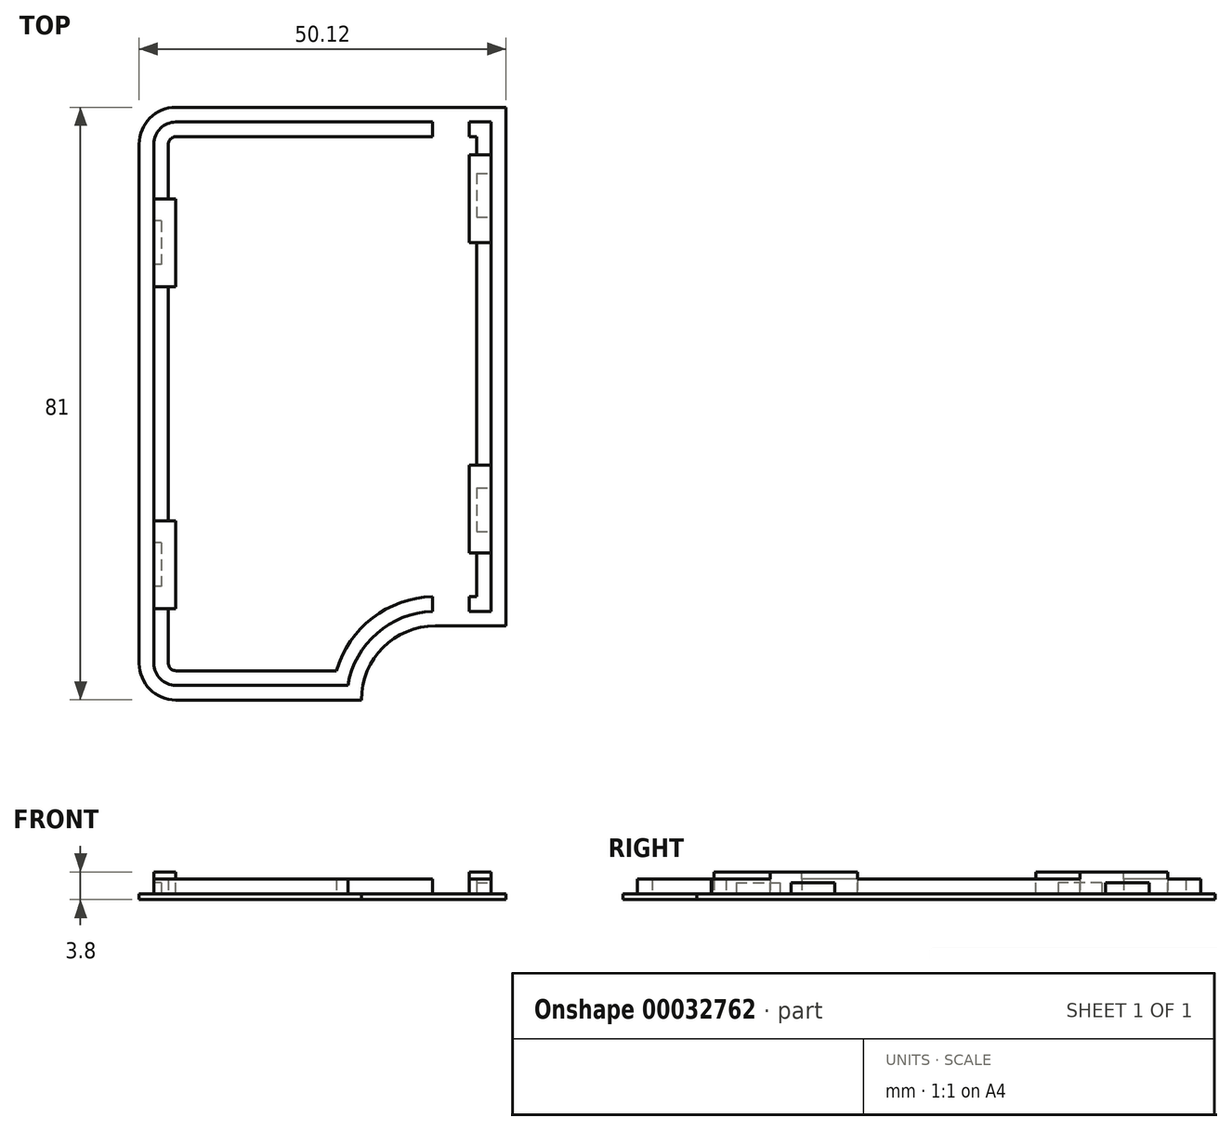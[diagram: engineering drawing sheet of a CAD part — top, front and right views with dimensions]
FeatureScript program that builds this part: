
annotation { "Feature Type Name" : "Feature", "Feature Type Description" : "" }
export const myFeature = defineFeature(function(context is Context, id is Id, definition is map)
    precondition{}
    {
        {
            var Q0;
            Q0=qCreatedBy(makeId("Top.planeOp"),FACE);
            var sketch = newSketch(context, id + "F0", { "sketchPlane" : qUnion([Q0])});
            skLineSegment(sketch, "E0.right", {"start": v(-29.22, 49.84) * mm, "end": v(-29.22, -31.16) * mm});
            skLineSegment(sketch, "E1.MirrorCS", {"start": v(11.28, -21.04) * mm, "end": v(20.9, -21.04) * mm});
            skLineSegment(sketch, "E2.MirrorCS", {"start": v(20.9, 49.84) * mm, "end": v(20.9, -21.04) * mm});
            skArc(sketch, "E3.MirrorCS", {"start": v(1.16, -31.16) * mm, "mid": v(4.12, -24) * mm, "end": v(11.28, -21.04) * mm});
            skLineSegment(sketch, "E4.MirrorCS", {"start": v(-29.22, 49.84) * mm, "end": v(20.9, 49.84) * mm});
            skLineSegment(sketch, "E5.MirrorCS", {"start": v(1.16, -31.16) * mm, "end": v(-29.22, -31.16) * mm});
            skSolve(sketch);
        }
        {
            var Q0;
            Q0=makeQuery(id+"F0.imprint","IMPRINT",FACE,{"disambiguationData":[TD([[makeQuery(id+"F0.imprint","IMPRINT",EDGE,{"derivedFrom":sQuery(id+"F0.wireOp",EDGE,"E0.right")}),1.0]])]});
            extrude(context, id + "F1", {"entities" : qUnion([Q0]), "depth" : .8 * mm});
        }
        {
            var Q0;
            Q0=makeQuery(id+"F1.opExtrude","SWEPT_EDGE",EDGE,{"disambiguationData":[OSD([sQuery(id+"F0.wireOp",EDGE,"E0.right"),sQuery(id+"F0.wireOp",EDGE,"E4.MirrorCS")])]});
            fillet(context, id + "F2", {"entities" : qUnion([Q0]), "radius" : 5 * mm, "tangentPropagation" : true, "allowEdgeOverflow" : false});
        }
        {
            var Q0;
            Q0=makeQuery(id+"F1.opExtrude","SWEPT_EDGE",EDGE,{"disambiguationData":[OSD([sQuery(id+"F0.wireOp",EDGE,"E0.right"),sQuery(id+"F0.wireOp",EDGE,"E5.MirrorCS")])]});
            fillet(context, id + "F3", {"entities" : qUnion([Q0]), "radius" : 5 * mm, "tangentPropagation" : true, "allowEdgeOverflow" : false});
        }
        {
            var Q0;
            Q0=makeQuery(id+"F1.opExtrude","CAP_FACE",FACE,{"disambiguationData":[OSD([sQuery(id+"F0.wireOp",EDGE,"E0.right"),sQuery(id+"F0.wireOp",EDGE,"E1.MirrorCS"),sQuery(id+"F0.wireOp",EDGE,"E2.MirrorCS"),sQuery(id+"F0.wireOp",EDGE,"E3.MirrorCS"),sQuery(id+"F0.wireOp",EDGE,"E4.MirrorCS"),sQuery(id+"F0.wireOp",EDGE,"E5.MirrorCS")])],"isStart":false});
            var sketch = newSketch(context, id + "F4", { "sketchPlane" : qUnion([Q0])});
            skLineSegment(sketch, "E6.0", {"start": v(-27.22, 44.84) * mm, "end": v(-27.22, -26.16) * mm});
            skArc(sketch, "E6.1", {"start": v(-24.22, 47.84) * mm, "mid": v(-26.34, 46.96) * mm, "end": v(-27.22, 44.84) * mm});
            skLineSegment(sketch, "E6.2", {"start": v(-24.22, 47.84) * mm, "end": v(18.9, 47.84) * mm});
            skLineSegment(sketch, "E6.3", {"start": v(18.9, 47.84) * mm, "end": v(18.9, -19.04) * mm});
            skLineSegment(sketch, "E6.4", {"start": v(11.28, -19.04) * mm, "end": v(18.9, -19.04) * mm});
            skArc(sketch, "E6.5", {"start": v(-27.22, -26.16) * mm, "mid": v(-26.34, -28.28) * mm, "end": v(-24.22, -29.16) * mm});
            skArc(sketch, "E6.6", {"start": v(-0.68, -29.16) * mm, "mid": v(3.45, -21.9) * mm, "end": v(11.28, -19.04) * mm});
            skLineSegment(sketch, "E6.7", {"start": v(-0.68, -29.16) * mm, "end": v(-24.22, -29.16) * mm});
            skSolve(sketch);
        }
        {
            var Q0;
            Q0=makeQuery(id+"F4.imprint","IMPRINT",FACE,{"disambiguationData":[TD([[makeQuery(id+"F4.imprint","IMPRINT",EDGE,{"derivedFrom":sQuery(id+"F4.wireOp",EDGE,"E6.0")}),1.0]])]});
            extrude(context, id + "F5", {"entities" : qUnion([Q0]), "operationType" : NewBodyOperationType.ADD, "depth" : 3 * mm});
        }
        {
            var Q0;
            Q0=makeQuery(id+"F5.opExtrude","SWEPT_FACE",FACE,{"disambiguationData":[OSD([sQuery(id+"F4.wireOp",EDGE,"E6.0")])]});
            var sketch = newSketch(context, id + "F6", { "sketchPlane" : qUnion([Q0])});
            skLineSegment(sketch, "E7", {"start": v(-9.34, 0.8) * mm, "end": v(-9.34, 3.8) * mm, "construction": true});
            skLineSegment(sketch, "E8", {"start": v(-9.34, 2.3) * mm, "end": v(-28.34, 2.3) * mm, "construction": true});
            skLineSegment(sketch, "E9", {"start": v(-9.34, 2.3) * mm, "end": v(9.66, 2.3) * mm, "construction": true});
            skLineSegment(sketch, "E10.bottom", {"start": v(-34.34, 2.3) * mm, "end": v(-28.34, 2.3) * mm});
            skLineSegment(sketch, "E10.top", {"start": v(-34.34, 0.8) * mm, "end": v(-28.34, 0.8) * mm});
            skLineSegment(sketch, "E10.left", {"start": v(-34.34, 2.3) * mm, "end": v(-34.34, 0.8) * mm});
            skLineSegment(sketch, "E10.right", {"start": v(-28.34, 2.3) * mm, "end": v(-28.34, 0.8) * mm});
            skLineSegment(sketch, "E11.bottom", {"start": v(15.66, 2.3) * mm, "end": v(9.66, 2.3) * mm});
            skLineSegment(sketch, "E11.top", {"start": v(15.66, 0.8) * mm, "end": v(9.66, 0.8) * mm});
            skLineSegment(sketch, "E11.left", {"start": v(15.66, 2.3) * mm, "end": v(15.66, 0.8) * mm});
            skLineSegment(sketch, "E11.right", {"start": v(9.66, 2.3) * mm, "end": v(9.66, 0.8) * mm});
            skSolve(sketch);
        }
        {
            var Q0;
            Q0=makeQuery(id+"F5.opExtrude","SWEPT_FACE",FACE,{"disambiguationData":[OSD([sQuery(id+"F4.wireOp",EDGE,"E6.3")])]});
            var sketch = newSketch(context, id + "F7", { "sketchPlane" : qUnion([Q0])});
            skSolve(sketch);
        }
        {
            var Q0;
            {var subQ0=sQuery(id+"F4.wireOp",EDGE,"E6.3");Q0=makeQuery(id+"F7.imprint","IMPRINT",FACE,{"disambiguationData":[TD([[makeQuery(id+"F7.imprint","IMPRINT",EDGE,{"derivedFrom":makeQuery(id+"F5.opExtrude","CAP_EDGE",EDGE,{"disambiguationData":[OSD([subQ0])],"isStart":false})}),1.0]])]});}
            var sketch = newSketch(context, id + "F8", { "sketchPlane" : qUnion([Q0])});
            skLineSegment(sketch, "E12.bottom", {"start": v(-8.16, 2.3) * mm, "end": v(-2.16, 2.3) * mm});
            skLineSegment(sketch, "E12.top", {"start": v(-8.16, 0.8) * mm, "end": v(-2.16, 0.8) * mm});
            skLineSegment(sketch, "E12.left", {"start": v(-8.16, 2.3) * mm, "end": v(-8.16, 0.8) * mm});
            skLineSegment(sketch, "E12.right", {"start": v(-2.16, 2.3) * mm, "end": v(-2.16, 0.8) * mm});
            skLineSegment(sketch, "E13.bottom", {"start": v(34.84, 2.3) * mm, "end": v(40.84, 2.3) * mm});
            skLineSegment(sketch, "E13.top", {"start": v(34.84, 0.8) * mm, "end": v(40.84, 0.8) * mm});
            skLineSegment(sketch, "E13.left", {"start": v(34.84, 2.3) * mm, "end": v(34.84, 0.8) * mm});
            skLineSegment(sketch, "E13.right", {"start": v(40.84, 2.3) * mm, "end": v(40.84, 0.8) * mm});
            skSolve(sketch);
        }
        {
            var Q0;
            Q0 = qSketchRegion(id + "F8", true);
            extrude(context, id + "F9", {"entities" : qUnion([Q0]), "operationType" : NewBodyOperationType.REMOVE, "oppositeDirection" : true, "depth" : 2 * mm});
        }
        {
            var Q0;
            Q0=makeQuery(id+"F5.opExtrude","CAP_FACE",FACE,{"disambiguationData":[OSD([sQuery(id+"F4.wireOp",EDGE,"E6.0"),sQuery(id+"F4.wireOp",EDGE,"E6.1"),sQuery(id+"F4.wireOp",EDGE,"E6.2"),sQuery(id+"F4.wireOp",EDGE,"E6.3"),sQuery(id+"F4.wireOp",EDGE,"E6.4"),sQuery(id+"F4.wireOp",EDGE,"E6.5"),sQuery(id+"F4.wireOp",EDGE,"E6.6"),sQuery(id+"F4.wireOp",EDGE,"E6.7")])],"isStart":false});
            var sketch = newSketch(context, id + "F10", { "sketchPlane" : qUnion([Q0])});
            skLineSegment(sketch, "E14.bottom", {"start": v(-27.22, -18.66) * mm, "end": v(-24.22, -18.66) * mm});
            skLineSegment(sketch, "E14.top", {"start": v(-27.22, -6.66) * mm, "end": v(-24.22, -6.66) * mm});
            skLineSegment(sketch, "E14.right", {"start": v(-24.22, -18.66) * mm, "end": v(-24.22, -6.66) * mm});
            skLineSegment(sketch, "E15.bottom", {"start": v(-27.22, 25.34) * mm, "end": v(-24.22, 25.34) * mm});
            skLineSegment(sketch, "E15.top", {"start": v(-27.22, 37.34) * mm, "end": v(-24.22, 37.34) * mm});
            skLineSegment(sketch, "E15.right", {"start": v(-24.22, 25.34) * mm, "end": v(-24.22, 37.34) * mm});
            skLineSegment(sketch, "E16.bottom", {"start": v(15.9, -11.04) * mm, "end": v(18.9, -11.04) * mm});
            skLineSegment(sketch, "E16.top", {"start": v(15.9, 0.96) * mm, "end": v(18.9, 0.96) * mm});
            skLineSegment(sketch, "E16.left", {"start": v(15.9, -11.04) * mm, "end": v(15.9, 0.96) * mm});
            skLineSegment(sketch, "E17.bottom", {"start": v(15.9, 31.34) * mm, "end": v(18.9, 31.34) * mm});
            skLineSegment(sketch, "E17.top", {"start": v(15.9, 43.34) * mm, "end": v(18.9, 43.34) * mm});
            skLineSegment(sketch, "E17.left", {"start": v(15.9, 31.34) * mm, "end": v(15.9, 43.34) * mm});
            skSolve(sketch);
        }
        {
            var Q0;
            {var subQ6=sQuery(id+"F10.wireOp",EDGE,"E14.bottom");Q0=makeQuery(id+"F10.imprint","IMPRINT",FACE,{"disambiguationData":[TD([[makeQuery(id+"F10.imprint","IMPRINT",EDGE,{"derivedFrom":subQ6}),-1.0]])]});}
            extrude(context, id + "F11", {"entities" : qUnion([Q0]), "operationType" : NewBodyOperationType.REMOVE, "oppositeDirection" : true, "depth" : 1.5 * mm});
        }
        {
            var Q0;
            {var subQ0=sQuery(id+"F4.wireOp",EDGE,"E6.2");var subQ1=sQuery(id+"F4.wireOp",EDGE,"E6.4");var subQ2=sQuery(id+"F10.wireOp",EDGE,"E17.top");var subQ3=sQuery(id+"F10.wireOp",EDGE,"E17.left");var subQ4=sQuery(id+"F4.wireOp",EDGE,"E6.3");var subQ5=sQuery(id+"F10.wireOp",EDGE,"E16.left");var subQ6=sQuery(id+"F10.wireOp",EDGE,"E16.top");var subQ7=sQuery(id+"F10.wireOp",EDGE,"E17.bottom");var subQ8=sQuery(id+"F10.wireOp",EDGE,"E16.bottom");Q0=makeQuery(id+"FbkqSHNZKuOhvot_1.boolean.opBoolean","SPLIT",FACE,{"disambiguationData":[TD([makeQuery(id+"F5.opExtrude","SWEPT_FACE",FACE,{"disambiguationData":[OSD([subQ4])]})])],"derivedFrom":makeQuery(id+"F11.boolean.opBoolean","COPY",FACE,{"derivedFrom":makeQuery(id+"F11.opExtrude","CAP_FACE",FACE,{"disambiguationData":[OSD([sQuery(id+"F4.wireOp",EDGE,"E6.0"),sQuery(id+"F4.wireOp",EDGE,"E6.1"),subQ0,subQ4,subQ1,sQuery(id+"F4.wireOp",EDGE,"E6.5"),sQuery(id+"F4.wireOp",EDGE,"E6.6"),sQuery(id+"F4.wireOp",EDGE,"E6.7"),sQuery(id+"F10.wireOp",EDGE,"E14.bottom"),sQuery(id+"F10.wireOp",EDGE,"E14.top"),sQuery(id+"F10.wireOp",EDGE,"E14.right"),sQuery(id+"F10.wireOp",EDGE,"E15.bottom"),sQuery(id+"F10.wireOp",EDGE,"E15.top"),sQuery(id+"F10.wireOp",EDGE,"E15.right"),subQ8,subQ6,subQ5,subQ7,subQ2,subQ3])],"isStart":false})})});}
            var Q1;
            {var subQ2=sQuery(id+"F8.wireOp",EDGE,"E13.top");var subQ3=sQuery(id+"F0.wireOp",EDGE,"E3.MirrorCS");var subQ4=sQuery(id+"F0.wireOp",EDGE,"E2.MirrorCS");var subQ5=sQuery(id+"F0.wireOp",EDGE,"E1.MirrorCS");var subQ6=sQuery(id+"F0.wireOp",EDGE,"E0.right");var subQ7=sQuery(id+"F0.wireOp",EDGE,"E4.MirrorCS");var subQ8=sQuery(id+"F0.wireOp",EDGE,"E5.MirrorCS");Q1=makeQuery(id+"FbkqSHNZKuOhvot_1.boolean.opBoolean","MERGE",FACE,{"derivedFrom":[makeQuery(id+"F1ftWp3afHHN7Bv_1.boolean.opBoolean","SPLIT",FACE,{"disambiguationData":[TD([makeQuery(id+"F1.opExtrude","SWEPT_FACE",FACE,{"disambiguationData":[OSD([subQ6])]})])],"derivedFrom":makeQuery(id+"F9.boolean.opBoolean","MERGE",FACE,{"derivedFrom":[makeQuery(id+"F1.opExtrude","CAP_FACE",FACE,{"disambiguationData":[OSD([subQ6,subQ5,subQ4,subQ3,subQ7,subQ8])],"isStart":false}),makeQuery(id+"F9.opExtrude","SWEPT_FACE",FACE,{"disambiguationData":[OSD([sQuery(id+"F8.wireOp",EDGE,"E12.top")])]}),makeQuery(id+"F9.opExtrude","SWEPT_FACE",FACE,{"disambiguationData":[OSD([subQ2])]})]})}),makeQuery(id+"FbkqSHNZKuOhvot_1.opExtrude","CAP_FACE",FACE,{"disambiguationData":[OSD([sQuery(id+"FVtTkqiu5xKcEQb_1.wireOp",EDGE,"mb8N7D4M-YfVz-ZY3y-VdnK-RlEoSl1ozBKI.bottom"),sQuery(id+"FVtTkqiu5xKcEQb_1.wireOp",EDGE,"mb8N7D4M-YfVz-ZY3y-VdnK-RlEoSl1ozBKI.top"),sQuery(id+"FVtTkqiu5xKcEQb_1.wireOp",EDGE,"mb8N7D4M-YfVz-ZY3y-VdnK-RlEoSl1ozBKI.left"),sQuery(id+"FVtTkqiu5xKcEQb_1.wireOp",EDGE,"mb8N7D4M-YfVz-ZY3y-VdnK-RlEoSl1ozBKI.right")])],"isStart":false})]});}
            extrude(context, id + "F12", {"entities" : qUnion([Q0]), "operationType" : NewBodyOperationType.REMOVE, "endBound" : BoundingType.UP_TO_SURFACE, "oppositeDirection" : true, "endBoundEntityFace" : qUnion([Q1]), "depth" : 25 * mm});
        }
        {
            var Q0;
            Q0 = qSketchRegion(id + "F6", true);
            extrude(context, id + "F13", {"entities" : qUnion([Q0]), "operationType" : NewBodyOperationType.REMOVE, "oppositeDirection" : true, "depth" : 1 * mm});
        }
        {
            var Q0;
            Q0=makeQuery(id+"F13.boolean.opBoolean","MERGE",FACE,{"derivedFrom":[makeQuery(id+"F12.boolean.opBoolean","MERGE",FACE,{"derivedFrom":[makeQuery(id+"F9.boolean.opBoolean","MERGE",FACE,{"derivedFrom":[makeQuery(id+"F1.opExtrude","CAP_FACE",FACE,{"disambiguationData":[OSD([sQuery(id+"F0.wireOp",EDGE,"E0.right"),sQuery(id+"F0.wireOp",EDGE,"E1.MirrorCS"),sQuery(id+"F0.wireOp",EDGE,"E2.MirrorCS"),sQuery(id+"F0.wireOp",EDGE,"E3.MirrorCS"),sQuery(id+"F0.wireOp",EDGE,"E4.MirrorCS"),sQuery(id+"F0.wireOp",EDGE,"E5.MirrorCS")])],"isStart":false}),makeQuery(id+"F9.opExtrude","SWEPT_FACE",FACE,{"disambiguationData":[OSD([sQuery(id+"F8.wireOp",EDGE,"E12.top")])]}),makeQuery(id+"F9.opExtrude","SWEPT_FACE",FACE,{"disambiguationData":[OSD([sQuery(id+"F8.wireOp",EDGE,"E13.top")])]})]}),makeQuery(id+"F12.opExtrude","CAP_FACE",FACE,{"disambiguationData":[OSD([sQuery(id+"F4.wireOp",EDGE,"E6.0"),sQuery(id+"F4.wireOp",EDGE,"E6.1"),sQuery(id+"F4.wireOp",EDGE,"E6.2"),sQuery(id+"F4.wireOp",EDGE,"E6.3"),sQuery(id+"F4.wireOp",EDGE,"E6.4"),sQuery(id+"F4.wireOp",EDGE,"E6.5"),sQuery(id+"F4.wireOp",EDGE,"E6.6"),sQuery(id+"F4.wireOp",EDGE,"E6.7"),sQuery(id+"F10.wireOp",EDGE,"E14.bottom"),sQuery(id+"F10.wireOp",EDGE,"E14.top"),sQuery(id+"F10.wireOp",EDGE,"E14.right"),sQuery(id+"F10.wireOp",EDGE,"E15.bottom"),sQuery(id+"F10.wireOp",EDGE,"E15.top"),sQuery(id+"F10.wireOp",EDGE,"E15.right"),sQuery(id+"F10.wireOp",EDGE,"E16.bottom"),sQuery(id+"F10.wireOp",EDGE,"E16.top"),sQuery(id+"F10.wireOp",EDGE,"E16.left"),sQuery(id+"F10.wireOp",EDGE,"E17.bottom"),sQuery(id+"F10.wireOp",EDGE,"E17.top"),sQuery(id+"F10.wireOp",EDGE,"E17.left")])],"isStart":false})]}),makeQuery(id+"F13.opExtrude","SWEPT_FACE",FACE,{"disambiguationData":[OSD([sQuery(id+"F6.wireOp",EDGE,"E10.top")])]}),makeQuery(id+"F13.opExtrude","SWEPT_FACE",FACE,{"disambiguationData":[OSD([sQuery(id+"F6.wireOp",EDGE,"E11.top")])]})]});
            var sketch = newSketch(context, id + "F14", { "sketchPlane" : qUnion([Q0])});
            skLineSegment(sketch, "E18.0", {"start": v(-0.68, -29.16) * mm, "end": v(-24.22, -29.16) * mm});
            skLineSegment(sketch, "E19.0", {"start": v(15.9, -19.04) * mm, "end": v(18.9, -19.04) * mm});
            skLineSegment(sketch, "E20.0", {"start": v(18.9, 47.84) * mm, "end": v(18.9, 43.34) * mm});
            skLineSegment(sketch, "E21.0", {"start": v(-24.22, 47.84) * mm, "end": v(10.9, 47.84) * mm});
            skLineSegment(sketch, "E22.0", {"start": v(-27.22, 44.84) * mm, "end": v(-27.22, 37.34) * mm});
            skArc(sketch, "E23.0", {"start": v(-27.22, -26.16) * mm, "mid": v(-26.34, -28.28) * mm, "end": v(-24.22, -29.16) * mm});
            skArc(sketch, "E24.0", {"start": v(-24.22, 47.84) * mm, "mid": v(-26.34, 46.96) * mm, "end": v(-27.22, 44.84) * mm});
            skLineSegment(sketch, "E25.trimOffspring", {"start": v(-27.22, -18.66) * mm, "end": v(-27.22, -26.16) * mm});
            skLineSegment(sketch, "E26.0", {"start": v(-2.26, -27.16) * mm, "end": v(-24.22, -27.16) * mm});
            skLineSegment(sketch, "E27.0", {"start": v(15.9, -17.04) * mm, "end": v(16.9, -17.04) * mm});
            skLineSegment(sketch, "E28.0", {"start": v(16.9, 45.84) * mm, "end": v(16.9, 43.34) * mm});
            skLineSegment(sketch, "E29.0", {"start": v(-24.22, 45.84) * mm, "end": v(10.9, 45.84) * mm});
            skArc(sketch, "E30.0", {"start": v(-24.22, 45.84) * mm, "mid": v(-24.92, 45.54) * mm, "end": v(-25.22, 44.84) * mm});
            skLineSegment(sketch, "E31.0", {"start": v(-25.22, -18.66) * mm, "end": v(-25.22, -26.16) * mm});
            skArc(sketch, "E32.0", {"start": v(-25.22, -26.16) * mm, "mid": v(-24.92, -26.87) * mm, "end": v(-24.22, -27.16) * mm});
            skLineSegment(sketch, "E33.0", {"start": v(-25.22, 44.84) * mm, "end": v(-25.22, 37.34) * mm});
            skLineSegment(sketch, "E34", {"start": v(-27.22, 25.34) * mm, "end": v(-25.22, 25.34) * mm});
            skLineSegment(sketch, "E35", {"start": v(-27.22, 37.34) * mm, "end": v(-25.22, 37.34) * mm});
            skLineSegment(sketch, "E36.trimOffspring", {"start": v(-25.22, 25.34) * mm, "end": v(-25.22, -6.66) * mm});
            skLineSegment(sketch, "E37.trimOffspring", {"start": v(-27.22, 25.34) * mm, "end": v(-27.22, -6.66) * mm});
            skLineSegment(sketch, "E38", {"start": v(-27.22, -6.66) * mm, "end": v(-25.22, -6.66) * mm});
            skLineSegment(sketch, "E39", {"start": v(-27.22, -18.66) * mm, "end": v(-25.22, -18.66) * mm});
            skLineSegment(sketch, "E40", {"start": v(16.9, -11.04) * mm, "end": v(18.9, -11.04) * mm});
            skLineSegment(sketch, "E41", {"start": v(16.9, 0.96) * mm, "end": v(18.9, 0.96) * mm});
            skLineSegment(sketch, "E42", {"start": v(16.9, 31.34) * mm, "end": v(18.9, 31.34) * mm});
            skLineSegment(sketch, "E43", {"start": v(16.9, 43.34) * mm, "end": v(18.9, 43.34) * mm});
            skLineSegment(sketch, "E44.trimOffspring", {"start": v(16.9, 31.34) * mm, "end": v(16.9, 0.96) * mm});
            skLineSegment(sketch, "E45.trimOffspring", {"start": v(16.9, -11.04) * mm, "end": v(16.9, -17.04) * mm});
            skLineSegment(sketch, "E46.trimOffspring", {"start": v(18.9, -11.04) * mm, "end": v(18.9, -19.04) * mm});
            skLineSegment(sketch, "E47.trimOffspring", {"start": v(18.9, 31.34) * mm, "end": v(18.9, 0.96) * mm});
            skArc(sketch, "E48.0", {"start": v(-0.68, -29.16) * mm, "mid": v(3.3, -22.03) * mm, "end": v(10.9, -19.04) * mm});
            skArc(sketch, "E49.trimOffspring", {"start": v(-2.26, -27.16) * mm, "mid": v(2.67, -19.96) * mm, "end": v(10.9, -17.04) * mm});
            skLineSegment(sketch, "E50.left", {"start": v(10.9, 47.84) * mm, "end": v(10.9, 45.84) * mm});
            skLineSegment(sketch, "E50.right", {"start": v(15.9, 47.84) * mm, "end": v(15.9, 45.84) * mm});
            skLineSegment(sketch, "E51.trimOffspring", {"start": v(10.9, -17.04) * mm, "end": v(10.9, -19.04) * mm});
            skLineSegment(sketch, "E52.trimOffspring", {"start": v(15.9, -17.04) * mm, "end": v(15.9, -19.04) * mm});
            skLineSegment(sketch, "E53.trimOffspring", {"start": v(15.9, 47.84) * mm, "end": v(18.9, 47.84) * mm});
            skLineSegment(sketch, "E54.trimOffspring", {"start": v(15.9, 45.84) * mm, "end": v(16.9, 45.84) * mm});
            skSolve(sketch);
        }
        {
            var Q0;
            Q0 = qSketchRegion(id + "F14", true);
            extrude(context, id + "F15", {"entities" : qUnion([Q0]), "operationType" : NewBodyOperationType.ADD, "depth" : 2 * mm});
        }
    });
